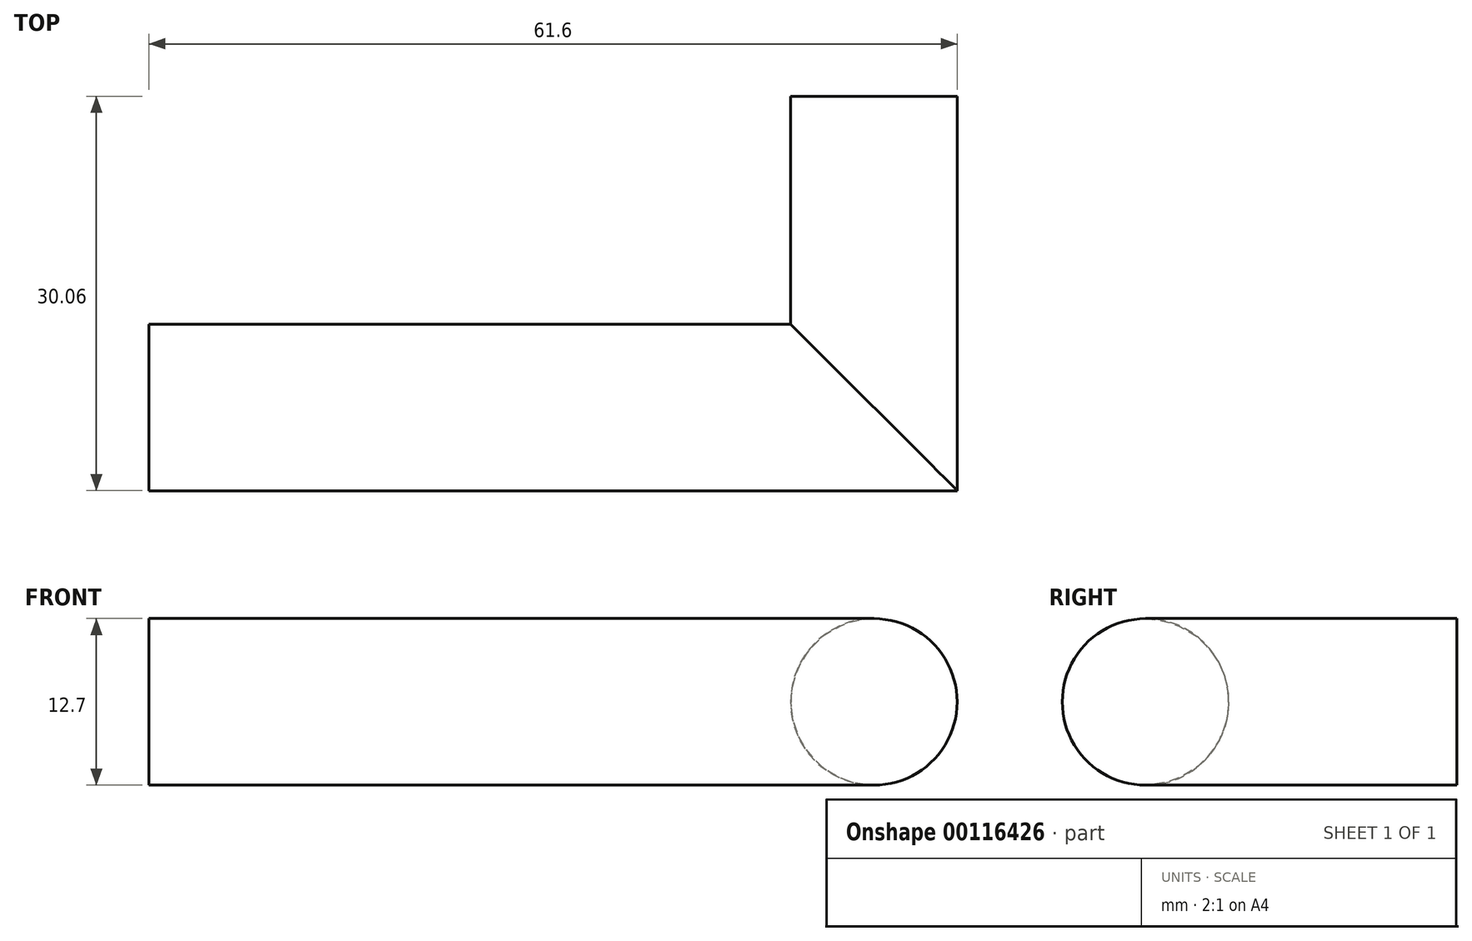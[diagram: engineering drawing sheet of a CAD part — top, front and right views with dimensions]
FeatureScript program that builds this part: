
annotation { "Feature Type Name" : "Feature", "Feature Type Description" : "" }
export const myFeature = defineFeature(function(context is Context, id is Id, definition is map)
    precondition{}
    {
        {
            var Q0;
            Q0=qCreatedBy(makeId("Front.planeOp"),FACE);
            var sketch = newSketch(context, id + "F0", { "sketchPlane" : qUnion([Q0])});
            skCircle(sketch, "E0", {"center": v(0, 0) * mm, "radius": 6.35 * mm});
            skSolve(sketch);
        }
        {
            var Q0;
            Q0=makeQuery(id+"F0.imprint","IMPRINT",FACE,{"disambiguationData":[TD([[makeQuery(id+"F0.imprint","IMPRINT",EDGE,{"derivedFrom":sQuery(id+"F0.wireOp",EDGE,"E0")}),1.0]])]});
            extrude(context, id + "F1", {"entities" : qUnion([Q0]), "depth" : 12.7 * mm});
        }
        {
            var Q0;
            Q0=qCreatedBy(makeId("Top.planeOp"),FACE);
            var sketch = newSketch(context, id + "F2", { "sketchPlane" : qUnion([Q0])});
            skLineSegment(sketch, "E1", {"start": v(0, -14.85) * mm, "end": v(0, -23.71) * mm});
            skLineSegment(sketch, "E2", {"start": v(-57.4, -23.71) * mm, "end": v(0, -23.71) * mm});
            skSolve(sketch);
        }
        {
            var Q0;
            Q0=makeQuery(id+"F1.opExtrude","CAP_FACE",FACE,{"disambiguationData":[OSD([sQuery(id+"F0.wireOp",EDGE,"E0")])],"isStart":false});
            var Q1;
            Q1=sQuery(id+"F2.wireOp",EDGE,"E1");
            var Q2;
            Q2=sQuery(id+"F2.wireOp",EDGE,"E2");
            sweep(context, id + "F3", {"operationType" : NewBodyOperationType.ADD, "profiles" : qUnion([Q0]), "path" : qUnion([Q1, Q2])});
        }
    });
